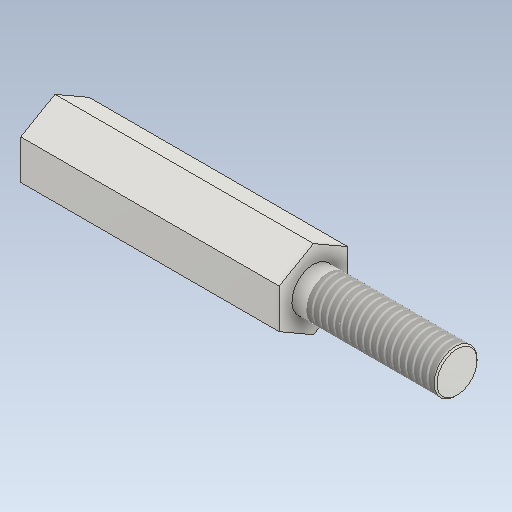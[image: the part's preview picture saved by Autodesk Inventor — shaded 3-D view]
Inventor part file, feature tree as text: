
AUTODESK INVENTOR PART (.ipt)
format: ipt  version: 2021 (Build 250183000, 183)  size: 140,288 bytes
history: native  units: mm
features: other x5, thread x4, chamfer x2, revolve x1
ambient origin geometry x6: Origin, XZ Plane, XY Plane, X Axis, Y Axis, Z Axis
bodies: Solid1 (feature_tree)
feature tree (12):
  revolve  "Revolution1"  [1 undecoded]
  other  "N-Side1"
  thread  "Thread2"  [1 undecoded]
  thread  "Thread4"  [1 undecoded]
  other  "Start Plane"
  other  "Origin point"
  other  "Main Sketch"
  other  "iFeature1:1"
  thread  "Thread1"  [1 undecoded]
  chamfer  "Chamfer1"  [1 undecoded]
  thread  "Thread3"  [1 undecoded]
  chamfer  "Chamfer2"  Distance=0.1mm Angle=45.0deg
note: 6 required parameter values undecoded (feature->parameter linkage not recoverable at this tier; creation-order binding heuristic only, values carry confidence <= 0.55)